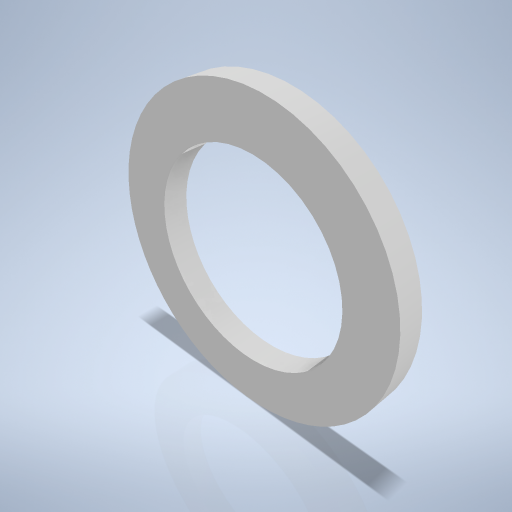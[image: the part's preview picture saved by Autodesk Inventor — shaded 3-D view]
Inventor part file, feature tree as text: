
AUTODESK INVENTOR PART (.ipt)
format: ipt  version: 2024.2 (Build 282272000, 272)  size: 238,080 bytes
history: native  units: mm
features: extrude x1, sketch x1
ambient origin geometry x8: Origin, YZ Plane, XZ Plane, XY Plane, X Axis, Y Axis, Z Axis, Center Point
bodies: Volumenkörper1 (feature_tree)
feature tree (2):
  extrude  "Extrusion1"  Depth=2.0mm
  sketch  "Skizze1"  dims[d0=24.0mm d1=16.0mm d2=2.0mm d3=0.0mm]
